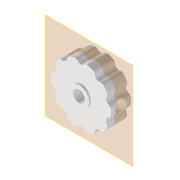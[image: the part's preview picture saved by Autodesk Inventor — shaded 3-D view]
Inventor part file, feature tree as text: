
AUTODESK INVENTOR PART (.ipt)
format: ipt  version: 2022 (Build 260153000, 153)  size: 175,616 bytes
history: native  units: mm
features: extrude x4, sketch x4, plane x1, fillet x1, pattern_circular x1
ambient origin geometry x8: Origin, YZ Plane, XZ Plane, XY Plane, X Axis, Y Axis, Z Axis, Center Point
bodies: Volumenkörper1 (feature_tree)
feature tree (11):
  extrude  "Extrusion1"  Depth=15.0mm
  plane  "Arbeitsebene1"
  extrude  "Extrusion2"  Depth=5.0mm TaperAngle=0.0deg
  extrude  "Extrusion4"  Depth=0.5mm TaperAngle=0.0deg
  fillet  "Rundung2"  Radius=9.599311mm
  pattern_circular  "Runde Anordnung3"  [2 undecoded]
  extrude  "Extrusion5"  Depth=2.5mm TaperAngle=360.0deg
  sketch  "Skizze1"  dims[d0=2.9mm d1=15.0mm]
  sketch  "Skizze2"  dims[d2=5.0mm d3=0.0mm d6=5.0mm d7=0.0mm]
  sketch  "Skizze5"  dims[d14=5.0mm d15=0.5mm d16=0.0mm d17=9.599311mm]
  sketch  "Skizze6"  dims[d18=21.816616mm d22=1.0mm d23=100.0mm d24=360.0deg d26=2.5mm d27=2.8mm d28=0.0mm d29=0.0mm]
note: 2 required parameter values undecoded (feature->parameter linkage not recoverable at this tier; creation-order binding heuristic only, values carry confidence <= 0.55)
